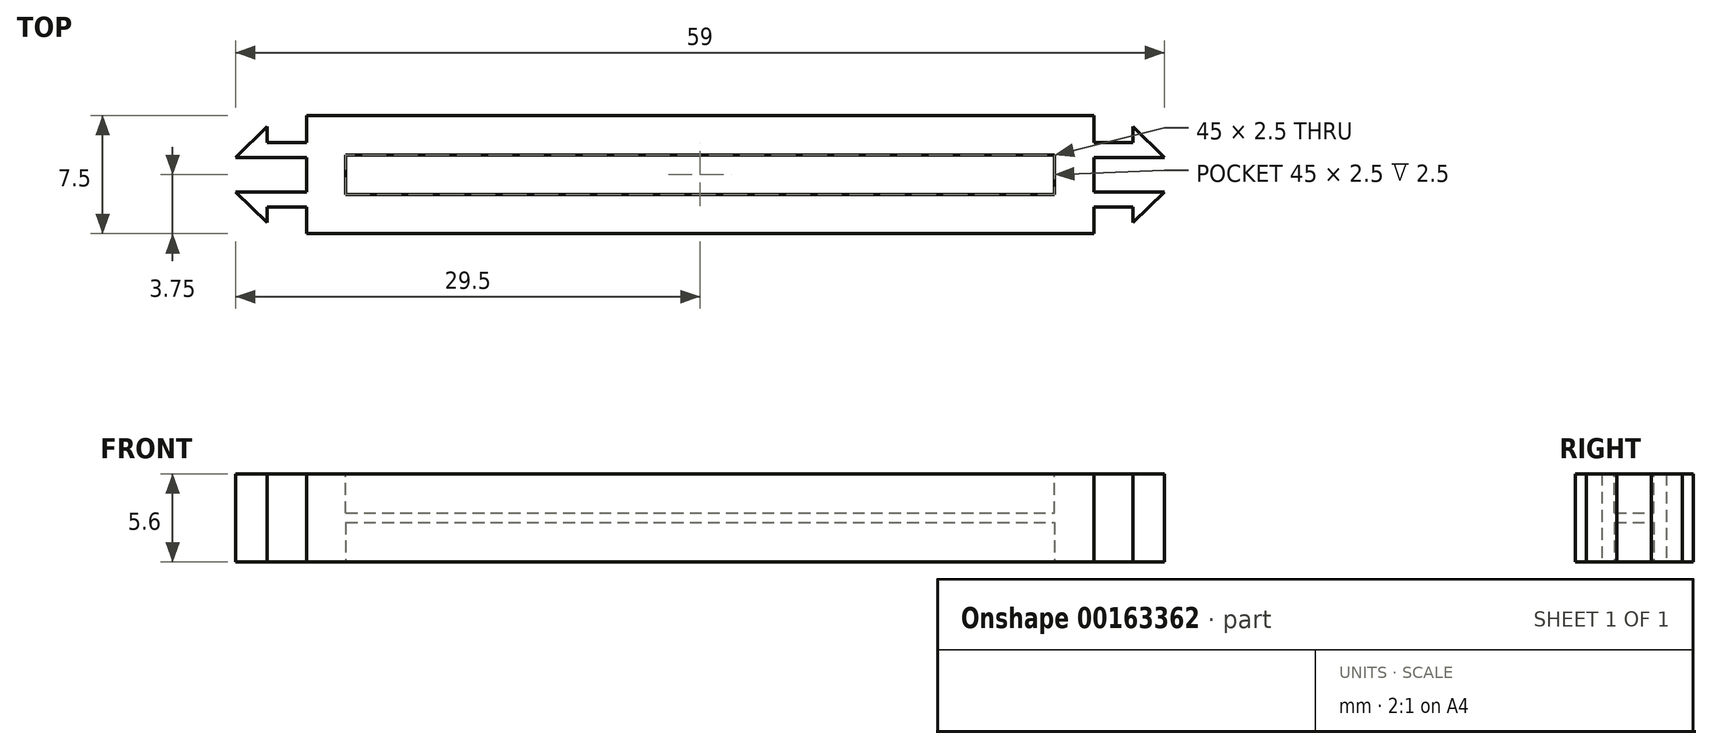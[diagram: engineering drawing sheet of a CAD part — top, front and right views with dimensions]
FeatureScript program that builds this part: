
annotation { "Feature Type Name" : "Feature", "Feature Type Description" : "" }
export const myFeature = defineFeature(function(context is Context, id is Id, definition is map)
    precondition{}
    {
        {
            var Q0;
            Q0=qCreatedBy(makeId("Top.planeOp"),FACE);
            var sketch = newSketch(context, id + "F0", { "sketchPlane" : qUnion([Q0])});
            skLineSegment(sketch, "E0", {"start": v(0, 3.75) * mm, "end": v(-25, 3.75) * mm});
            skLineSegment(sketch, "E1", {"start": v(-25, -3.75) * mm, "end": v(0, -3.75) * mm});
            skLineSegment(sketch, "E2", {"start": v(0, 3.75) * mm, "end": v(0, -3.75) * mm, "construction": true});
            skLineSegment(sketch, "E3", {"start": v(-25, 3.75) * mm, "end": v(-25, 2.05) * mm});
            skLineSegment(sketch, "E4", {"start": v(-25, -3.75) * mm, "end": v(-25, -2.05) * mm});
            skLineSegment(sketch, "E5", {"start": v(-25, -2.05) * mm, "end": v(-27.5, -2.05) * mm});
            skLineSegment(sketch, "E6", {"start": v(-25, 2.05) * mm, "end": v(-27.5, 2.05) * mm});
            skLineSegment(sketch, "E7", {"start": v(-29.5, 1.1) * mm, "end": v(-25, 1.1) * mm});
            skLineSegment(sketch, "E8", {"start": v(-25, 1.1) * mm, "end": v(-25, -1.1) * mm});
            skLineSegment(sketch, "E9", {"start": v(-25, -1.1) * mm, "end": v(-29.5, -1.1) * mm});
            skPoint(sketch, "E10", {"position": v(-25, 0) * mm});
            skLineSegment(sketch, "E11", {"start": v(-27.5, 2.05) * mm, "end": v(-27.5, 3.05) * mm});
            skLineSegment(sketch, "E12", {"start": v(-27.5, -2.05) * mm, "end": v(-27.5, -3.05) * mm});
            skLineSegment(sketch, "E13", {"start": v(-27.5, 3.05) * mm, "end": v(-29.5, 1.1) * mm});
            skLineSegment(sketch, "E14", {"start": v(-29.5, 1.1) * mm, "end": v(-29.5, -1.1) * mm, "construction": true});
            skLineSegment(sketch, "E15", {"start": v(-27.5, 2.05) * mm, "end": v(-27.5, -2.05) * mm, "construction": true});
            skLineSegment(sketch, "E16", {"start": v(-29.5, -1.1) * mm, "end": v(-27.5, -3.05) * mm});
            skLineSegment(sketch, "E17.MirrorCS", {"start": v(0, 3.75) * mm, "end": v(25, 3.75) * mm});
            skLineSegment(sketch, "E18.MirrorCS", {"start": v(25, 3.75) * mm, "end": v(25, 2.05) * mm});
            skLineSegment(sketch, "E19.MirrorCS", {"start": v(25, 2.05) * mm, "end": v(27.5, 2.05) * mm});
            skLineSegment(sketch, "E20.MirrorCS", {"start": v(27.5, 2.05) * mm, "end": v(27.5, 3.05) * mm});
            skLineSegment(sketch, "E21.MirrorCS", {"start": v(27.5, 3.05) * mm, "end": v(29.5, 1.1) * mm});
            skLineSegment(sketch, "E22.MirrorCS", {"start": v(29.5, 1.1) * mm, "end": v(25, 1.1) * mm});
            skLineSegment(sketch, "E23.MirrorCS", {"start": v(25, 1.1) * mm, "end": v(25, -1.1) * mm});
            skLineSegment(sketch, "E24.MirrorCS", {"start": v(25, -1.1) * mm, "end": v(29.5, -1.1) * mm});
            skLineSegment(sketch, "E25.MirrorCS", {"start": v(29.5, -1.1) * mm, "end": v(27.5, -3.05) * mm});
            skLineSegment(sketch, "E26.MirrorCS", {"start": v(27.5, -2.05) * mm, "end": v(27.5, -3.05) * mm});
            skLineSegment(sketch, "E27.MirrorCS", {"start": v(25, -2.05) * mm, "end": v(27.5, -2.05) * mm});
            skLineSegment(sketch, "E28.MirrorCS", {"start": v(25, -3.75) * mm, "end": v(25, -2.05) * mm});
            skLineSegment(sketch, "E29.MirrorCS", {"start": v(25, -3.75) * mm, "end": v(0, -3.75) * mm});
            skSolve(sketch);
        }
        {
            var Q0;
            Q0 = qSketchRegion(id + "F0", true);
            extrude(context, id + "F1", {"entities" : qUnion([Q0]), "depth" : 5.6 * mm});
        }
        {
            var Q0;
            Q0=makeQuery(id+"F1.opExtrude","CAP_FACE",FACE,{"disambiguationData":[OSD([sQuery(id+"F0.wireOp",EDGE,"E0"),sQuery(id+"F0.wireOp",EDGE,"zfWpewbX-yxJe-N6jc-GUxu-f3MnnSvkJUu6"),sQuery(id+"F0.wireOp",EDGE,"wysgG7iT-laDj-qhrx-5T2V-g0xNqW3rQVZk"),sQuery(id+"F0.wireOp",EDGE,"uQTP36Ky-zSSg-0Tp2-VpBM-qWYeH3VO8ThV"),sQuery(id+"F0.wireOp",EDGE,"IBOapmpm-XnTn-xskc-8Qh8-Xi5eDCzvym5P"),sQuery(id+"F0.wireOp",EDGE,"NXc8xNNb-WfXu-LAOv-sAiN-w9NP4JhsXg1n"),sQuery(id+"F0.wireOp",EDGE,"h0Dwil2A-FZ6o-pJmb-XJ0l-v2fExJ1VvxLc"),sQuery(id+"F0.wireOp",EDGE,"6iJk6k7J-P9qi-detK-Yd0T-LV98UKP2MSjE"),sQuery(id+"F0.wireOp",EDGE,"fc6ced6f-3ecf-4532-80a7-46be7dd3c0270.MirrorCS"),sQuery(id+"F0.wireOp",EDGE,"67e91d4d-277a-4f97-aa02-21e9a55ade870.MirrorCS"),sQuery(id+"F0.wireOp",EDGE,"bc09f364-ae71-4a48-be01-c54f67c3a75a0.MirrorCS"),sQuery(id+"F0.wireOp",EDGE,"85b5edc2-271c-43df-906c-00e1c2372e950.MirrorCS"),sQuery(id+"F0.wireOp",EDGE,"cb5455a6-27cc-4fca-9384-caf212e223dd0.MirrorCS"),sQuery(id+"F0.wireOp",EDGE,"1383d608-a064-44ed-87c7-87c26c0c378e0.MirrorCS"),sQuery(id+"F0.wireOp",EDGE,"561397c7-cedb-4237-a9df-32b7675c45360.MirrorCS"),sQuery(id+"F0.wireOp",EDGE,"0b72c48d-af96-456b-97aa-ece9813336df0.MirrorCS"),sQuery(id+"F0.wireOp",EDGE,"64e4c5a7-5aa1-40a5-9b56-0fafc66c094f0.MirrorCS"),sQuery(id+"F0.wireOp",EDGE,"5a206232-2377-4310-aeeb-78d22da80a110.MirrorCS"),sQuery(id+"F0.wireOp",EDGE,"d0b358aa-6ed5-4407-995a-c6e6d18fdf760.MirrorCS"),sQuery(id+"F0.wireOp",EDGE,"fd8f50c4-3b71-44ab-a797-bd8743f3e5890.MirrorCS"),sQuery(id+"F0.wireOp",EDGE,"7dfdd7b7-86e4-4716-ba37-13ed81f5819f0.MirrorCS"),sQuery(id+"F0.wireOp",EDGE,"702b9861-355d-42cd-a5f2-f0de6c3845e30.MirrorCS"),sQuery(id+"F0.wireOp",EDGE,"969d549c-9fbf-41d7-acd6-bd4d9082ed4f0.MirrorCS"),sQuery(id+"F0.wireOp",EDGE,"2bcc8568-de4e-4add-8158-caeace92670b0.MirrorCS"),sQuery(id+"F0.wireOp",EDGE,"bb14c967-96ac-4cbb-a8df-faac90f36b760.MirrorCS"),sQuery(id+"F0.wireOp",EDGE,"b182940c-a0f0-48cb-b5cc-0b90ac2e3ad50.MirrorCS"),sQuery(id+"F0.wireOp",EDGE,"48aff3ea-bbf0-4daf-8532-2b19afb0a2f10.MirrorCS"),sQuery(id+"F0.wireOp",EDGE,"b80f0973-bff2-488a-9801-55719254c6990.MirrorCS"),sQuery(id+"F0.wireOp",EDGE,"27b7c14b-62bc-4f11-8d88-7bb65e15acea0.MirrorCS"),sQuery(id+"F0.wireOp",EDGE,"4a54e6b2-31b9-43f0-a5a4-14cba57476300.MirrorCS"),sQuery(id+"F0.wireOp",EDGE,"578ec57d-1ff0-41ab-b6cd-15d689548c9c0.MirrorCS"),sQuery(id+"F0.wireOp",EDGE,"c9ee28b0-03b0-41b8-a535-fd35aaaf28830.MirrorCS")])],"isStart":false});
            var sketch = newSketch(context, id + "F2", { "sketchPlane" : qUnion([Q0])});
            skLineSegment(sketch, "E30.0", {"start": v(22.5, 1) * mm, "end": v(22.5, 1.25) * mm});
            skLineSegment(sketch, "E30.1", {"start": v(22.5, -2.2) * mm, "end": v(22.5, 1) * mm});
            skLineSegment(sketch, "E30.2", {"start": v(22.5, 1.25) * mm, "end": v(-22.5, 1.25) * mm});
            skLineSegment(sketch, "E30.3", {"start": v(22.5, -2.2) * mm, "end": v(22.5, -1.25) * mm});
            skLineSegment(sketch, "E30.4", {"start": v(-22.5, 2.2) * mm, "end": v(-22.5, 1.25) * mm});
            skLineSegment(sketch, "E30.5", {"start": v(-22.5, 2.2) * mm, "end": v(-22.5, -1) * mm});
            skLineSegment(sketch, "E30.6", {"start": v(-22.5, -1) * mm, "end": v(-22.5, -1.25) * mm});
            skLineSegment(sketch, "E30.7", {"start": v(-22.5, -1.25) * mm, "end": v(22.5, -1.25) * mm});
            skSolve(sketch);
        }
        {
            var Q0;
            Q0 = qSketchRegion(id + "F2", true);
            extrude(context, id + "F3", {"entities" : qUnion([Q0]), "operationType" : NewBodyOperationType.REMOVE, "oppositeDirection" : true, "depth" : 2.5 * mm});
        }
        {
            var Q0;
            Q0=makeQuery(id+"F1.opExtrude","CAP_FACE",FACE,{"disambiguationData":[OSD([sQuery(id+"F0.wireOp",EDGE,"E0"),sQuery(id+"F0.wireOp",EDGE,"zfWpewbX-yxJe-N6jc-GUxu-f3MnnSvkJUu6"),sQuery(id+"F0.wireOp",EDGE,"wysgG7iT-laDj-qhrx-5T2V-g0xNqW3rQVZk"),sQuery(id+"F0.wireOp",EDGE,"uQTP36Ky-zSSg-0Tp2-VpBM-qWYeH3VO8ThV"),sQuery(id+"F0.wireOp",EDGE,"IBOapmpm-XnTn-xskc-8Qh8-Xi5eDCzvym5P"),sQuery(id+"F0.wireOp",EDGE,"NXc8xNNb-WfXu-LAOv-sAiN-w9NP4JhsXg1n"),sQuery(id+"F0.wireOp",EDGE,"h0Dwil2A-FZ6o-pJmb-XJ0l-v2fExJ1VvxLc"),sQuery(id+"F0.wireOp",EDGE,"6iJk6k7J-P9qi-detK-Yd0T-LV98UKP2MSjE"),sQuery(id+"F0.wireOp",EDGE,"fc6ced6f-3ecf-4532-80a7-46be7dd3c0270.MirrorCS"),sQuery(id+"F0.wireOp",EDGE,"67e91d4d-277a-4f97-aa02-21e9a55ade870.MirrorCS"),sQuery(id+"F0.wireOp",EDGE,"bc09f364-ae71-4a48-be01-c54f67c3a75a0.MirrorCS"),sQuery(id+"F0.wireOp",EDGE,"85b5edc2-271c-43df-906c-00e1c2372e950.MirrorCS"),sQuery(id+"F0.wireOp",EDGE,"cb5455a6-27cc-4fca-9384-caf212e223dd0.MirrorCS"),sQuery(id+"F0.wireOp",EDGE,"1383d608-a064-44ed-87c7-87c26c0c378e0.MirrorCS"),sQuery(id+"F0.wireOp",EDGE,"561397c7-cedb-4237-a9df-32b7675c45360.MirrorCS"),sQuery(id+"F0.wireOp",EDGE,"0b72c48d-af96-456b-97aa-ece9813336df0.MirrorCS"),sQuery(id+"F0.wireOp",EDGE,"64e4c5a7-5aa1-40a5-9b56-0fafc66c094f0.MirrorCS"),sQuery(id+"F0.wireOp",EDGE,"5a206232-2377-4310-aeeb-78d22da80a110.MirrorCS"),sQuery(id+"F0.wireOp",EDGE,"d0b358aa-6ed5-4407-995a-c6e6d18fdf760.MirrorCS"),sQuery(id+"F0.wireOp",EDGE,"fd8f50c4-3b71-44ab-a797-bd8743f3e5890.MirrorCS"),sQuery(id+"F0.wireOp",EDGE,"7dfdd7b7-86e4-4716-ba37-13ed81f5819f0.MirrorCS"),sQuery(id+"F0.wireOp",EDGE,"702b9861-355d-42cd-a5f2-f0de6c3845e30.MirrorCS"),sQuery(id+"F0.wireOp",EDGE,"969d549c-9fbf-41d7-acd6-bd4d9082ed4f0.MirrorCS"),sQuery(id+"F0.wireOp",EDGE,"2bcc8568-de4e-4add-8158-caeace92670b0.MirrorCS"),sQuery(id+"F0.wireOp",EDGE,"bb14c967-96ac-4cbb-a8df-faac90f36b760.MirrorCS"),sQuery(id+"F0.wireOp",EDGE,"b182940c-a0f0-48cb-b5cc-0b90ac2e3ad50.MirrorCS"),sQuery(id+"F0.wireOp",EDGE,"48aff3ea-bbf0-4daf-8532-2b19afb0a2f10.MirrorCS"),sQuery(id+"F0.wireOp",EDGE,"b80f0973-bff2-488a-9801-55719254c6990.MirrorCS"),sQuery(id+"F0.wireOp",EDGE,"27b7c14b-62bc-4f11-8d88-7bb65e15acea0.MirrorCS"),sQuery(id+"F0.wireOp",EDGE,"4a54e6b2-31b9-43f0-a5a4-14cba57476300.MirrorCS"),sQuery(id+"F0.wireOp",EDGE,"578ec57d-1ff0-41ab-b6cd-15d689548c9c0.MirrorCS"),sQuery(id+"F0.wireOp",EDGE,"c9ee28b0-03b0-41b8-a535-fd35aaaf28830.MirrorCS")])],"isStart":true});
            var sketch = newSketch(context, id + "F4", { "sketchPlane" : qUnion([Q0])});
            skLineSegment(sketch, "E31.0", {"start": v(-22.5, 0.4) * mm, "end": v(-22.5, -1.25) * mm});
            skLineSegment(sketch, "E31.1", {"start": v(22.5, -1.25) * mm, "end": v(22.5, -0.4) * mm});
            skLineSegment(sketch, "E31.2", {"start": v(22.5, -0.4) * mm, "end": v(22.5, 1.25) * mm});
            skLineSegment(sketch, "E31.3", {"start": v(-22.5, -1.25) * mm, "end": v(22.5, -1.25) * mm});
            skLineSegment(sketch, "E31.4", {"start": v(22.5, 1.25) * mm, "end": v(-22.5, 1.25) * mm});
            skLineSegment(sketch, "E31.5", {"start": v(-22.5, 1.25) * mm, "end": v(-22.5, 0.4) * mm});
            skSolve(sketch);
        }
        {
            var Q0;
            Q0 = qSketchRegion(id + "F4", true);
            extrude(context, id + "F5", {"entities" : qUnion([Q0]), "operationType" : NewBodyOperationType.REMOVE, "oppositeDirection" : true, "depth" : 2.5 * mm});
        }
    });
